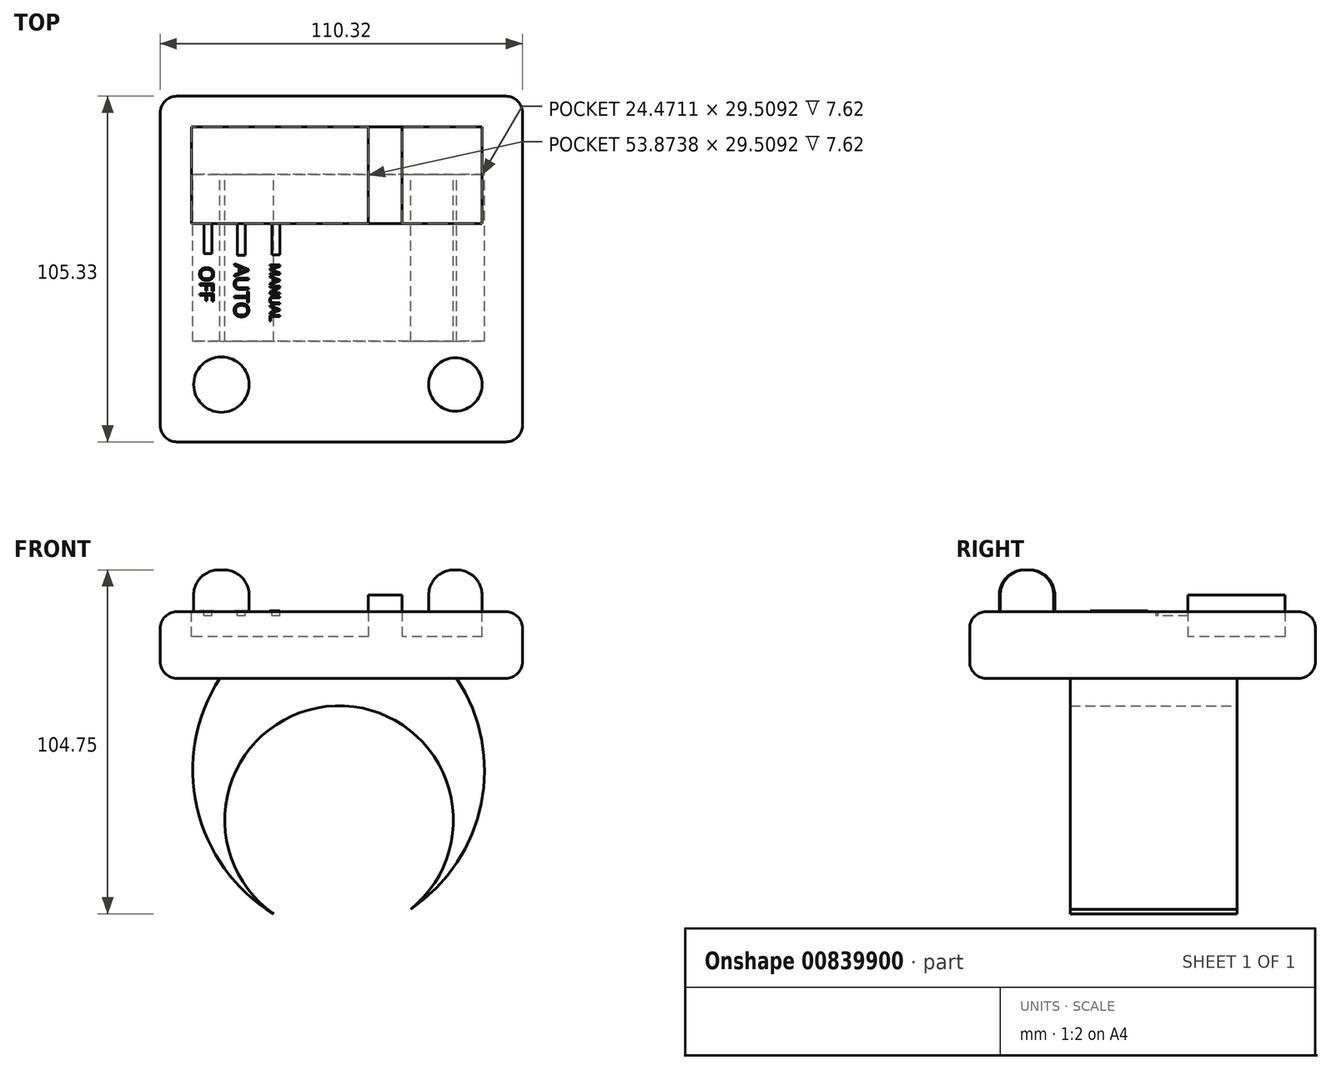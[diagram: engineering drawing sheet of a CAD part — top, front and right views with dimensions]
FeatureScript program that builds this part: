
annotation { "Feature Type Name" : "Feature", "Feature Type Description" : "" }
export const myFeature = defineFeature(function(context is Context, id is Id, definition is map)
    precondition{}
    {
        {
            var Q0;
            Q0=qCreatedBy(makeId("Front.planeOp"),FACE);
            var sketch = newSketch(context, id + "F0", { "sketchPlane" : qUnion([Q0])});
            skArc(sketch, "E0", {"start": v(12.48, -33.82) * mm, "mid": v(-10.44, 28.16) * mm, "end": v(-29.28, -35.18) * mm});
            skLineSegment(sketch, "E1", {"start": v(-45.63, 36.55) * mm, "end": v(26.56, 36.55) * mm});
            skArc(sketch, "E2", {"start": v(-45.63, 36.55) * mm, "mid": v(-52.61, -2.77) * mm, "end": v(-29.28, -35.18) * mm});
            skArc(sketch, "E3", {"start": v(12.48, -33.82) * mm, "mid": v(34.02, -1.54) * mm, "end": v(26.56, 36.55) * mm});
            skSolve(sketch);
        }
        {
            var Q0;
            Q0 = qSketchRegion(id + "F0", true);
            extrude(context, id + "F1", {"entities" : qUnion([Q0]), "depth" : 50.8 * mm, "offsetDistance" : 25.4 * mm});
        }
        {
            var Q0;
            Q0=makeQuery(id+"F1.opExtrude","SWEPT_FACE",FACE,{"disambiguationData":[OSD([sQuery(id+"F0.wireOp",EDGE,"E1")])]});
            var sketch = newSketch(context, id + "F2", { "sketchPlane" : qUnion([Q0])});
            skLineSegment(sketch, "E4.bottom", {"start": v(46.53, 23.86) * mm, "end": v(-63.79, 23.86) * mm});
            skLineSegment(sketch, "E4.top", {"start": v(46.53, -81.47) * mm, "end": v(-63.79, -81.47) * mm});
            skLineSegment(sketch, "E4.left", {"start": v(46.53, 23.86) * mm, "end": v(46.53, -81.47) * mm});
            skLineSegment(sketch, "E4.right", {"start": v(-63.79, 23.86) * mm, "end": v(-63.79, -81.47) * mm});
            skSolve(sketch);
        }
        {
            var Q0;
            Q0 = qSketchRegion(id + "F2", true);
            extrude(context, id + "F3", {"entities" : qUnion([Q0]), "operationType" : NewBodyOperationType.ADD, "depth" : 20.32 * mm, "offsetDistance" : 25.4 * mm});
        }
        {
            var Q0;
            Q0=makeQuery(id+"F3.opExtrude","CAP_FACE",FACE,{"disambiguationData":[OSD([sQuery(id+"F2.wireOp",EDGE,"E4.bottom"),sQuery(id+"F2.wireOp",EDGE,"E4.top"),sQuery(id+"F2.wireOp",EDGE,"E4.left"),sQuery(id+"F2.wireOp",EDGE,"E4.right")])],"isStart":false});
            var sketch = newSketch(context, id + "F4", { "sketchPlane" : qUnion([Q0])});
            skCircle(sketch, "E5", {"center": v(26.1, -63.99) * mm, "radius": 8.12 * mm});
            skCircle(sketch, "E6", {"center": v(-45.17, -63.99) * mm, "radius": 8.44 * mm});
            skSolve(sketch);
        }
        {
            var Q0;
            Q0 = qSketchRegion(id + "F4", true);
            extrude(context, id + "F5", {"entities" : qUnion([Q0]), "operationType" : NewBodyOperationType.ADD, "depth" : 12.7 * mm, "offsetDistance" : 25.4 * mm});
        }
        {
            var Q0;
            Q0=makeQuery(id+"F5.opExtrude","CAP_EDGE",EDGE,{"disambiguationData":[OSD([sQuery(id+"F4.wireOp",EDGE,"E5")])],"isStart":false});
            var Q1;
            Q1=makeQuery(id+"F5.opExtrude","CAP_EDGE",EDGE,{"disambiguationData":[OSD([sQuery(id+"F4.wireOp",EDGE,"E6")])],"isStart":false});
            fillet(context, id + "F6", {"entities" : qUnion([Q0, Q1]), "radius" : 7.62 * mm, "tangentPropagation" : true, "allowEdgeOverflow" : false});
        }
        {
            var Q0;
            Q0=makeQuery(id+"F3.opExtrude","CAP_FACE",FACE,{"disambiguationData":[OSD([sQuery(id+"F2.wireOp",EDGE,"E4.bottom"),sQuery(id+"F2.wireOp",EDGE,"E4.top"),sQuery(id+"F2.wireOp",EDGE,"E4.left"),sQuery(id+"F2.wireOp",EDGE,"E4.right")])],"isStart":false});
            var sketch = newSketch(context, id + "F7", { "sketchPlane" : qUnion([Q0])});
            skLineSegment(sketch, "E7.bottom", {"start": v(34.28, 14.55) * mm, "end": v(-54.25, 14.55) * mm});
            skLineSegment(sketch, "E7.top", {"start": v(34.28, -14.96) * mm, "end": v(-54.25, -14.96) * mm});
            skLineSegment(sketch, "E7.left", {"start": v(34.28, 14.55) * mm, "end": v(34.28, -14.96) * mm});
            skLineSegment(sketch, "E7.right", {"start": v(-54.25, 14.55) * mm, "end": v(-54.25, -14.96) * mm});
            skSolve(sketch);
        }
        {
            var Q0;
            Q0 = qSketchRegion(id + "F7", true);
            extrude(context, id + "F8", {"entities" : qUnion([Q0]), "operationType" : NewBodyOperationType.REMOVE, "oppositeDirection" : true, "depth" : 7.62 * mm, "offsetDistance" : 25.4 * mm});
        }
        {
            var Q0;
            Q0=makeQuery(id+"F8.boolean.opBoolean","COPY",FACE,{"derivedFrom":makeQuery(id+"F8.opExtrude","CAP_FACE",FACE,{"disambiguationData":[OSD([sQuery(id+"F7.wireOp",EDGE,"E7.bottom"),sQuery(id+"F7.wireOp",EDGE,"E7.top"),sQuery(id+"F7.wireOp",EDGE,"E7.left"),sQuery(id+"F7.wireOp",EDGE,"E7.right")])],"isStart":false})});
            var sketch = newSketch(context, id + "F9", { "sketchPlane" : qUnion([Q0])});
            skLineSegment(sketch, "E8.bottom", {"start": v(9.8, 14.55) * mm, "end": v(-0.38, 14.55) * mm});
            skLineSegment(sketch, "E8.top", {"start": v(9.8, -14.96) * mm, "end": v(-0.38, -14.96) * mm});
            skLineSegment(sketch, "E8.left", {"start": v(9.8, 14.55) * mm, "end": v(9.8, -14.96) * mm});
            skLineSegment(sketch, "E8.right", {"start": v(-0.38, 14.55) * mm, "end": v(-0.38, -14.96) * mm});
            skSolve(sketch);
        }
        {
            var Q0;
            Q0 = qSketchRegion(id + "F9", true);
            var Q1;
            Q1=makeQuery(id+"F9.imprint","IMPRINT",FACE,{"disambiguationData":[TD([[makeQuery(id+"F9.imprint","IMPRINT",EDGE,{"derivedFrom":sQuery(id+"F9.wireOp",EDGE,"E8.top")}),-1.0]])]});
            extrude(context, id + "F10", {"entities" : qUnion([Q0, Q1]), "operationType" : NewBodyOperationType.ADD, "depth" : 12.7 * mm, "offsetDistance" : 25.4 * mm});
        }
        {
            var Q0;
            Q0=makeQuery(id+"F3.opExtrude","SWEPT_EDGE",EDGE,{"disambiguationData":[OSD([sQuery(id+"F2.wireOp",EDGE,"E4.bottom"),sQuery(id+"F2.wireOp",EDGE,"E4.right")])]});
            var Q1;
            Q1=makeQuery(id+"F3.opExtrude","SWEPT_EDGE",EDGE,{"disambiguationData":[OSD([sQuery(id+"F2.wireOp",EDGE,"E4.top"),sQuery(id+"F2.wireOp",EDGE,"E4.right")])]});
            var Q2;
            Q2=makeQuery(id+"F3.opExtrude","SWEPT_EDGE",EDGE,{"disambiguationData":[OSD([sQuery(id+"F2.wireOp",EDGE,"E4.bottom"),sQuery(id+"F2.wireOp",EDGE,"E4.left")])]});
            var Q3;
            Q3=makeQuery(id+"F3.opExtrude","SWEPT_EDGE",EDGE,{"disambiguationData":[OSD([sQuery(id+"F2.wireOp",EDGE,"E4.top"),sQuery(id+"F2.wireOp",EDGE,"E4.left")])]});
            var Q4;
            Q4=makeQuery(id+"F3.opExtrude","CAP_EDGE",EDGE,{"disambiguationData":[OSD([sQuery(id+"F2.wireOp",EDGE,"E4.top")])],"isStart":false});
            var Q5;
            Q5=makeQuery(id+"F3.opExtrude","CAP_EDGE",EDGE,{"disambiguationData":[OSD([sQuery(id+"F2.wireOp",EDGE,"E4.right")])],"isStart":false});
            var Q6;
            Q6=makeQuery(id+"F3.opExtrude","CAP_EDGE",EDGE,{"disambiguationData":[OSD([sQuery(id+"F2.wireOp",EDGE,"E4.left")])],"isStart":true});
            var Q7;
            Q7=makeQuery(id+"F3.opExtrude","CAP_EDGE",EDGE,{"disambiguationData":[OSD([sQuery(id+"F2.wireOp",EDGE,"E4.bottom")])],"isStart":false});
            var Q8;
            Q8=makeQuery(id+"F3.opExtrude","CAP_EDGE",EDGE,{"disambiguationData":[OSD([sQuery(id+"F2.wireOp",EDGE,"E4.bottom")])],"isStart":true});
            var Q9;
            Q9=makeQuery(id+"F3.opExtrude","CAP_EDGE",EDGE,{"disambiguationData":[OSD([sQuery(id+"F2.wireOp",EDGE,"E4.left")])],"isStart":false});
            var Q10;
            Q10=makeQuery(id+"F3.opExtrude","CAP_EDGE",EDGE,{"disambiguationData":[OSD([sQuery(id+"F2.wireOp",EDGE,"E4.top")])],"isStart":true});
            var Q11;
            Q11=makeQuery(id+"F3.opExtrude","CAP_EDGE",EDGE,{"disambiguationData":[OSD([sQuery(id+"F2.wireOp",EDGE,"E4.right")])],"isStart":true});
            fillet(context, id + "F11", {"entities" : qUnion([Q0, Q1, Q2, Q3, Q4, Q5, Q6, Q7, Q8, Q9, Q10, Q11]), "radius" : 5.08 * mm, "tangentPropagation" : true, "allowEdgeOverflow" : false});
        }
        {
            var Q0;
            Q0=makeQuery(id+"F3.opExtrude","CAP_FACE",FACE,{"disambiguationData":[OSD([sQuery(id+"F2.wireOp",EDGE,"E4.bottom"),sQuery(id+"F2.wireOp",EDGE,"E4.top"),sQuery(id+"F2.wireOp",EDGE,"E4.left"),sQuery(id+"F2.wireOp",EDGE,"E4.right")])],"isStart":false});
            var sketch = newSketch(context, id + "F12", { "sketchPlane" : qUnion([Q0])});
            skLineSegment(sketch, "E9.bottom", {"start": v(-50.45, -14.96) * mm, "end": v(-48.02, -14.96) * mm});
            skLineSegment(sketch, "E9.top", {"start": v(-50.45, -24.05) * mm, "end": v(-48.02, -24.05) * mm});
            skLineSegment(sketch, "E9.left", {"start": v(-50.45, -14.96) * mm, "end": v(-50.45, -24.05) * mm});
            skLineSegment(sketch, "E9.right", {"start": v(-48.02, -14.96) * mm, "end": v(-48.02, -24.05) * mm});
            skLineSegment(sketch, "E10.bottom", {"start": v(-40.32, -14.96) * mm, "end": v(-37.9, -14.96) * mm});
            skLineSegment(sketch, "E10.top", {"start": v(-40.32, -24.65) * mm, "end": v(-37.9, -24.65) * mm});
            skLineSegment(sketch, "E10.left", {"start": v(-40.32, -14.96) * mm, "end": v(-40.32, -24.65) * mm});
            skLineSegment(sketch, "E10.right", {"start": v(-37.9, -14.96) * mm, "end": v(-37.9, -24.65) * mm});
            skPoint(sketch, "E11.oppositeSnap0", {"position": v(-27.31, -14.96) * mm});
            skLineSegment(sketch, "E11.bottom", {"start": v(-29.8, -14.96) * mm, "end": v(-27.31, -14.96) * mm});
            skLineSegment(sketch, "E11.top", {"start": v(-29.8, -24.45) * mm, "end": v(-27.31, -24.45) * mm});
            skLineSegment(sketch, "E11.left", {"start": v(-29.8, -14.96) * mm, "end": v(-29.8, -24.45) * mm});
            skLineSegment(sketch, "E11.right", {"start": v(-27.31, -14.96) * mm, "end": v(-27.31, -24.45) * mm});
            skSolve(sketch);
        }
        {
            var Q0;
            Q0 = qSketchRegion(id + "F12", true);
            extrude(context, id + "F13", {"entities" : qUnion([Q0]), "operationType" : NewBodyOperationType.REMOVE, "oppositeDirection" : true, "depth" : 1.27 * mm, "offsetDistance" : 25.4 * mm});
        }
        {
            var Q0;
            Q0=makeQuery(id+"F3.opExtrude","CAP_FACE",FACE,{"disambiguationData":[OSD([sQuery(id+"F2.wireOp",EDGE,"E4.bottom"),sQuery(id+"F2.wireOp",EDGE,"E4.top"),sQuery(id+"F2.wireOp",EDGE,"E4.left"),sQuery(id+"F2.wireOp",EDGE,"E4.right")])],"isStart":false});
            var sketch = newSketch(context, id + "F14", { "sketchPlane" : qUnion([Q0])});
            skText(sketch, "E12", { "text": "MANUAL", "fontName": "OpenSans-Regular.ttf"});
            const initialGuessF14  = {"E12": [-0.03043, -0.02708, 0, -1, 0.00305]};
            skSetInitialGuess(sketch, initialGuessF14);
            skSolve(sketch);
        }
        {
            var Q0;
            Q0 = qSketchRegion(id + "F14", true);
            extrude(context, id + "F15", {"entities" : qUnion([Q0]), "operationType" : NewBodyOperationType.ADD, "depth" : 0.25 * mm, "offsetDistance" : 25.4 * mm});
        }
        {
            var Q0;
            {var subQ0=sQuery(id+"F2.wireOp",EDGE,"E4.left");var subQ1=sQuery(id+"F2.wireOp",EDGE,"E4.top");var subQ2=sQuery(id+"F2.wireOp",EDGE,"E4.right");var subQ3=sQuery(id+"F2.wireOp",EDGE,"E4.bottom");Q0=makeQuery(id+"F15.boolean.opBoolean","SPLIT",FACE,{"disambiguationData":[TD([makeQuery(id+"F5.opExtrude","SWEPT_FACE",FACE,{"disambiguationData":[OSD([sQuery(id+"F4.wireOp",EDGE,"E5")])]})])],"derivedFrom":makeQuery(id+"F3.opExtrude","CAP_FACE",FACE,{"disambiguationData":[OSD([subQ3,subQ1,subQ0,subQ2])],"isStart":false})});}
            var sketch = newSketch(context, id + "F16", { "sketchPlane" : qUnion([Q0])});
            skText(sketch, "E13", { "text": "AUTO", "fontName": "OpenSans-Regular.ttf"});
            const initialGuessF16  = {"E13": [-0.04124, -0.02718, 0, -1, 0.00443]};
            skSetInitialGuess(sketch, initialGuessF16);
            skSolve(sketch);
        }
        {
            var Q0;
            Q0 = qSketchRegion(id + "F16", true);
            extrude(context, id + "F17", {"entities" : qUnion([Q0]), "operationType" : NewBodyOperationType.ADD, "depth" : 0.25 * mm, "offsetDistance" : 25.4 * mm});
        }
        {
            var Q0;
            {var subQ35=sQuery(id+"F2.wireOp",EDGE,"E4.right");var subQ36=sQuery(id+"F2.wireOp",EDGE,"E4.top");var subQ40=sQuery(id+"F2.wireOp",EDGE,"E4.left");var subQ49=sQuery(id+"F2.wireOp",EDGE,"E4.bottom");var subQ52=makeQuery(id+"F5.opExtrude","SWEPT_FACE",FACE,{"disambiguationData":[OSD([sQuery(id+"F4.wireOp",EDGE,"E5")])]});Q0=makeQuery(id+"F17.boolean.opBoolean","SPLIT",FACE,{"disambiguationData":[TD([subQ52])],"derivedFrom":makeQuery(id+"F15.boolean.opBoolean","SPLIT",FACE,{"disambiguationData":[TD([subQ52])],"derivedFrom":makeQuery(id+"F3.opExtrude","CAP_FACE",FACE,{"disambiguationData":[OSD([subQ49,subQ36,subQ40,subQ35])],"isStart":false})})});}
            var sketch = newSketch(context, id + "F18", { "sketchPlane" : qUnion([Q0])});
            skText(sketch, "E14", { "text": "OFF", "fontName": "OpenSans-Regular.ttf"});
            const initialGuessF18  = {"E14": [-0.05178, -0.02803, 0, -1, 0.00425]};
            skSetInitialGuess(sketch, initialGuessF18);
            skSolve(sketch);
        }
        {
            var Q0;
            Q0 = qSketchRegion(id + "F18", true);
            extrude(context, id + "F19", {"entities" : qUnion([Q0]), "operationType" : NewBodyOperationType.ADD, "depth" : 0.25 * mm, "offsetDistance" : 25.4 * mm});
        }
    });
